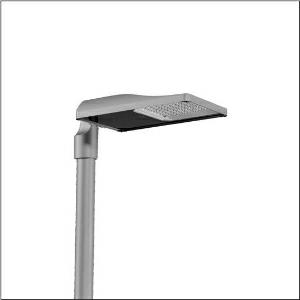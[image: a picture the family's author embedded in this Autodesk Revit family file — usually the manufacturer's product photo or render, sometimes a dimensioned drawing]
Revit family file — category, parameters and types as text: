
# Revit family: streetlight_sl_31_midi___pl52_5xh7h4aa08ma_ed53
name_source: partatom
category: Lighting Fixtures
units: mm (PartAtom-declared; Revit-internal decimal feet)

## family parameters
Cut with Voids When Loaded = No
Host = Face
Light Source = No
Part Type = Normal
Room Calculation Point = No
Round Connector Dimension = Use Diameter
Shared = No

## types (1)
- --- (1 x LED, 19840 lm, 145.3 W, 4000K)
    Apparent Load = 145 VA
    CIE Flux Codes = 27 59 98 100 100
    Color Rendering = 70
    Color Temperature = 4000K
    Default Elevation = 1800 mm
    Description = Streetlight SL 31 midi Easy LST mast luminaire for post-top, side-entry; light control with lens of PMMA; light distribution: PL52, direct asymmetric distribution, for standard-compliant lighting for roads and squares; LED: luminous flux: 19.840lm, light colour: 740, colour temperature: 4000K; luminous efficacy: 136,5lm/W; control: pre-setting: linear dimming characteristic, flexible luminous flux parameterisation, time-dependent luminous flux control, constant luminous flux control, power reduction, intelligent temperature release in ECG and LED module, overheat protection; luminaire housing, of diecast aluminium, Siteco® metallic grey (DB 702S), corrosivity category C5 high according to DIN EN ISO 12944; cover of toughened safety glass, transparent, opened without tools; mast flange of diecast aluminium, Siteco® metallic grey (DB 702S), spigot size: 76/60mm, mast flange included unmounted; with cable H07RN-F 3x 1.5mm², cable length: 10,5m, connection cable pre-assembled; mains connection: 220..240V, AC, 50/60Hz; power consumption (at start of service life): 145,3W / (at end of service life): 161,8W / (with reduced operation 50%): 61,1W; protection rating (complete): IP66; insulation class (complete): insulation class II (safety insulation); impact resistance: IK09; certification: CE, ENEC, ENEC+, VDE, UKCA; permissible operating ambient temperature for outdoor applications: -40..+50°C; packaging unit: 1 piece

Light Distribution: PL52
    Height = 79 mm
    Lamp = 1 x LED
    Lamp Light Flux = 19840 lm
    Lamp Power = 145.3 W
    Lamp count = 1
    Length = 577 mm
    Luminous efficacy = 137 lm/W
    Manufacturer = Siteco
    ModVariant = No
    Model = 5XH7H4AA08MA
    Number of Poles = 1
    OnlyDefault = Yes
    Power Factor = 1
    Product Name = Streetlight SL 31 midi | PL52
    Product group = mast luminaire | pylon top
    ProductGroupID = 6100
    Protection Class = Protection class II
    Protection Degree = IP 66
    RLX_Detail_Level = 1
    RLX_Emergency_Light_Flux = 0 lm
    RLX_Emergency_Type = 0
    RLX_Emergency_Type_DB = No
    RlxData = <blob elided: 52401 chars, md5=69547bb5>
    Socket = socket
    Standby Power = 0 W
    System Light Flux = 19841 lm
    System Power = 145 W
    Type Comments = factory setting: luminous flux: 100 % | dim-lin: 254 | 747 mA
    Type Image = l_1300317.jpg
    URL = http://relux.com
    VarID = @adj_054722
    Voltage = 0 V
    Weight = 0.00 kg
    Width = 362 mm

## geometry (parser evidence)
native form markers: Blend x4, Sweep x9
no freeform markers — native parametric forms only
